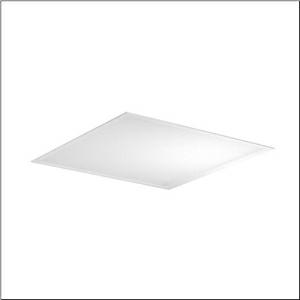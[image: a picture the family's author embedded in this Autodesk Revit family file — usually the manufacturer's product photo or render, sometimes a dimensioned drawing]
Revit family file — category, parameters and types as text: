
# Revit family: apollon_21_square_51mq12wc2454
name_source: partatom
category: Lighting Fixtures
units: mm (PartAtom-declared; Revit-internal decimal feet)

## family parameters
Cut with Voids When Loaded = No
Host = Face
Light Source = No
Part Type = Normal
Room Calculation Point = No
Round Connector Dimension = Use Diameter
Shared = No

## types (1)
- Apollon 21 square (1 x LED, 4200 lm, 24.7 W, 4000K)
    Apparent Load = 25 VA
    CIE Flux Codes = 60 87 97 100 100
    Color Rendering = 80
    Color Temperature = 4000K
    Default Elevation = 1800 mm
    Description = Apollon 21 square, office luminaire, primary optical cover: micro prismatic cover, of PMMA, CAT 2 (L<= 3000cd/m²), light emission: direct distribution, primary light characteristic: symmetric, installation type: lay-in mounting, LED, rated luminous flux: 4.200lm, luminous efficacy: 170lm/W, light colour: 840, colour temperature: 4000K, control gear: DALI 2, Multilumen, with terminal, 5-pole, mains connection: 220..240V, AC/DC, 0/50..60Hz, rated input power: 24.7W, suitable for self-contained emergency lighting element 59MQE002602A with integrated self-test function according to EN 60598-2-22, housing, of aluminium, coated, traffic white (RAL 9016), module: M600, length: 595mm, width: 595mm, height: 55mm, recess depth: 180mm, housing upper side, of sheet steel, galvanised, protection rating (complete): IP20, protection rating (lamp compartment, on room side): IP54, insulation class (complete): insulation class II (safety insulation), certification: CE, ENEC, impact resistance: IK03, permissible operating ambient temperature: -20..+45°C, permissible storage temperature: -40..+80°C, standard: EN 60598-2-22, packaging unit: 1 piece
    Height = 0 mm  [stored 0 ft]
    Lamp = 1 x LED
    Lamp Light Flux = 4200 lm
    Lamp Power = 24.7 W
    Lamp count = 1
    Length = 595 mm
    Luminous efficacy = 170 lm/W
    Manufacturer = Siteco
    ModVariant = No
    Model = 51MQ12WC2454
    Mounting Place = Ceiling
    Mounting Type = Recessed
    Number of Poles = 1
    OnlyDefault = Yes
    Power Factor = 1
    Product Name = Apollon 21 square
    Product group = office luminaire | ceiling recessed
    ProductGroupID = 400
    Protection Class = Protection class II
    Protection Degree = IP 20
    RLX_Detail_Level = 1
    RLX_Emergency_Light_Flux = 0 lm
    RLX_Emergency_Type = 0
    RLX_Emergency_Type_DB = No
    RlxData = <blob elided: 12713 chars, md5=5338a16d>
    Socket = socket
    Standby Power = 0 W
    System Light Flux = 4200 lm
    System Power = 25 W
    Type Comments = Product without accessories
    Type Image = l_1291049.jpg
    URL = http://relux.com
    VarID = ---
    Voltage = 0 V
    Weight = 0.00 kg
    Width = 595 mm

note: [stored X ft] marks values corroborated as IEEE doubles in the binary element streams (Revit-internal decimal feet)

## geometry (parser evidence)
native form markers: Sweep x10
no freeform markers — native parametric forms only
